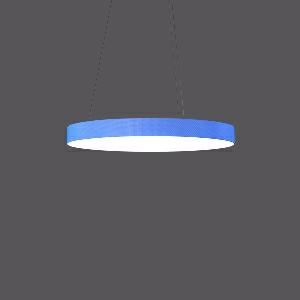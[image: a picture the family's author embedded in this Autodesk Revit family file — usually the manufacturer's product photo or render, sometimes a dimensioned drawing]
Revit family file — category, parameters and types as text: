
# Revit family: flatliner_slim_312284_002_1_9cab
name_source: partatom
category: Lighting Fixtures
units: mm (PartAtom-declared; Revit-internal decimal feet)

## family parameters
Cut with Voids When Loaded = No
Host = Face
Light Source = No
Part Type = Normal
Room Calculation Point = No
Round Connector Dimension = Use Diameter
Shared = No

## types (1)
- 982557.002 (1 x LED Modul 840, 2050 lm, 4000)
    Apparent Load = 27 VA
    CIE Flux Codes = 45 76 94 95 100
    Color Rendering = 80
    Color Temperature = 4000
    Default Elevation = 1800 mm
    Description = Series: FLATLINER SLIM
 Decorative pendant luminaire for interior decoration. Base luminaire prepared for the installation of fabric lampshade. Base and canopy: metal, powder-coated, white. 3-point steel cable suspension, steplessly adjustable. Special lengths available on request. Transparent connecting cable. Modular design: with the basic luminaire, a cylindrical fabric lampshade with a polycarbonate satin-finish diffuser must always be ordered separately. Fabric lampshade and diffuser can be assembled without the use of tools. 
Colour: white
Diameter: 418 mm
Height: 34 mm
Suspension length: 200-1300 mm
Lamp: LED exchangeable
Socket: without socket
Colour temperature: 4000K
Colour rendering index (CRI): 80
System power: 24 W
Rated luminous flux: 2050 lm
Luminous efficiency: 85 lm/W
Control gear: AC Strom, dim.Ph.an-/abschnitt
Protection class: I
Type of protection: IP 20
    Height = 34 mm  [stored 0.111549 ft]
    Lamp = 1 x LED Modul 840
    Lamp Light Flux = 2050 lm
    Lamp count = 1
    Length = 418 mm
    Lifetime = 50000 h
    Luminous efficacy = 76 lm/W
    Manufacturer = RZB
    ModVariant = No
    Model = 312284.002.1
    Mounting Place = Ceiling
    Mounting Type = Pendant
    Number of Poles = 1
    OnlyDefault = Yes
    Power Factor = 1
    Product Name = FLATLINER SLIM
    Product group = Pendant-Fabric lampshade luminaires
    ProductGroupID = 913
    Protection Class = Protection class I
    Protection Degree = IP 20
    RLX_Detail_Level = 1
    RLX_Emergency_Light_Flux = 0 lm
    RLX_Emergency_Type = 0
    RLX_Emergency_Type_DB = No
    RlxData = <blob elided: 24101 chars, md5=69d31ebd>
    Socket = socket
    Standby Power = 0 W
    System Light Flux = 2050 lm
    System Power = 27 W
    Type Image = 312288.002_982442.006_982444.002.jpg
    URL = http://relux.com
    VarID = 982557_002_b87f
    Voltage = 230 V
    Voltage Range = 220-240 V
    Weight = 0.00 kg
    Width = 0 mm  [stored 0 ft]

note: [stored X ft] marks values corroborated as IEEE doubles in the binary element streams (Revit-internal decimal feet)

## geometry (parser evidence)
native form markers: Blend x4, Sweep x12
no freeform markers — native parametric forms only
